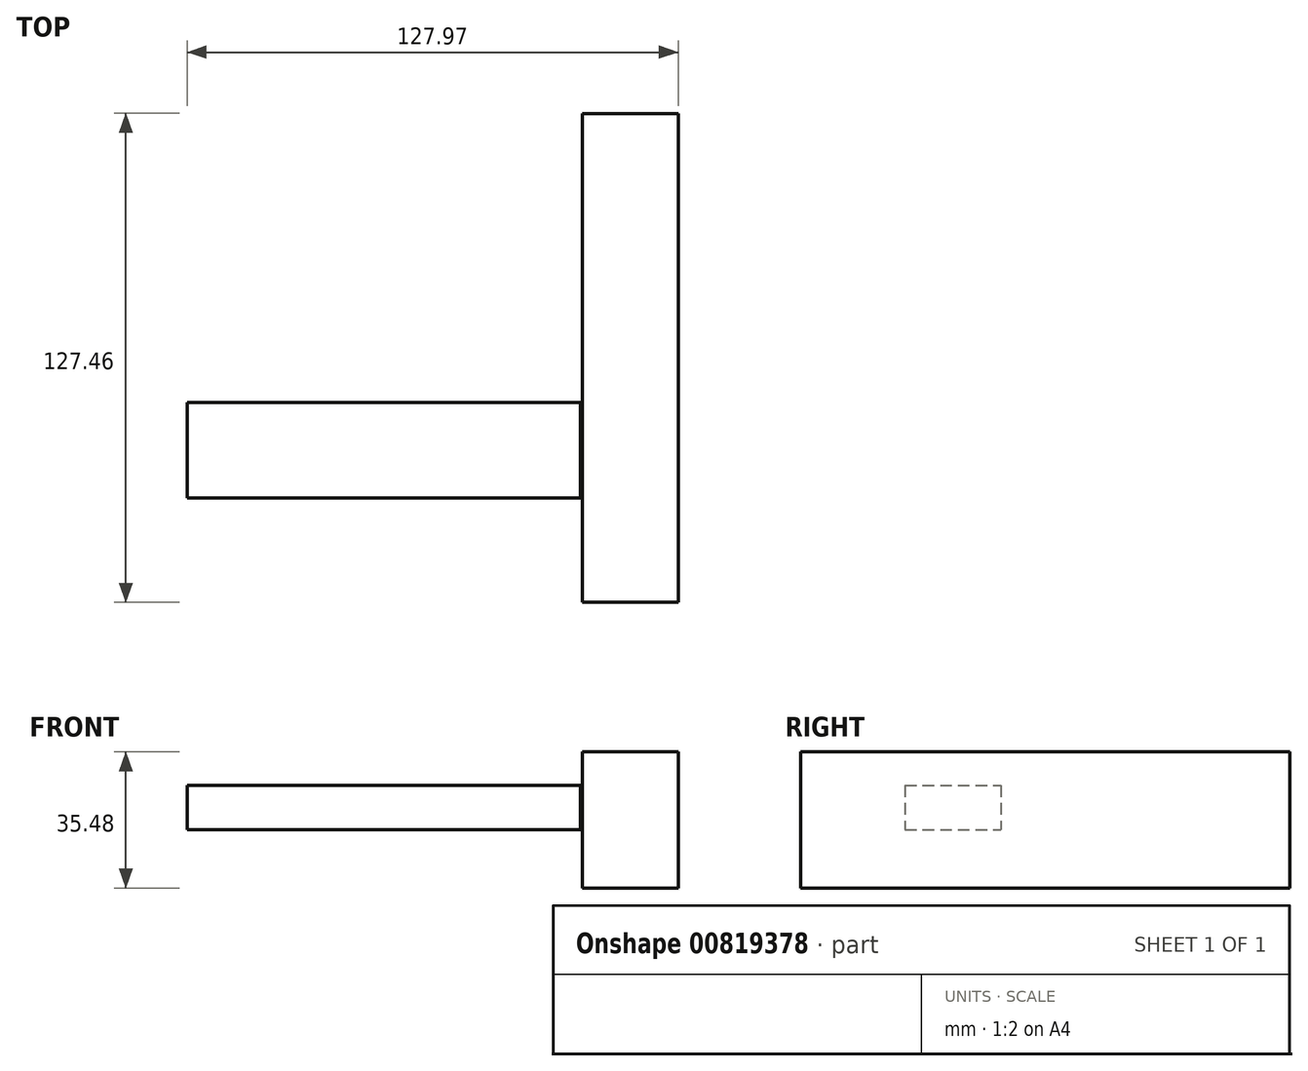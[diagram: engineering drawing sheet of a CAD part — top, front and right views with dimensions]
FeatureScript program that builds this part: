
annotation { "Feature Type Name" : "Feature", "Feature Type Description" : "" }
export const myFeature = defineFeature(function(context is Context, id is Id, definition is map)
    precondition{}
    {
        {
            var Q0;
            Q0=qCreatedBy(makeId("Right.planeOp"),FACE);
            var sketch = newSketch(context, id + "F0", { "sketchPlane" : qUnion([Q0])});
            skLineSegment(sketch, "E0.bottom", {"start": v(-52.14, 16.6) * mm, "end": v(75.32, 16.6) * mm});
            skLineSegment(sketch, "E0.top", {"start": v(-52.14, -18.9) * mm, "end": v(75.32, -18.9) * mm});
            skLineSegment(sketch, "E0.left", {"start": v(-52.14, 16.6) * mm, "end": v(-52.14, -18.9) * mm});
            skLineSegment(sketch, "E0.right", {"start": v(75.32, 16.6) * mm, "end": v(75.32, -18.9) * mm});
            skSolve(sketch);
        }
        {
            var Q0;
            Q0=makeQuery(id+"F0.imprint","IMPRINT",FACE,{"disambiguationData":[TD([[makeQuery(id+"F0.imprint","IMPRINT",EDGE,{"derivedFrom":sQuery(id+"F0.wireOp",EDGE,"E0.bottom")}),-1.0]])]});
            extrude(context, id + "F1", {"entities" : qUnion([Q0]), "endBound" : BoundingType.SYMMETRIC, "depth" : 25 * mm, "offsetDistance" : 25 * mm});
        }
        {
            var Q0;
            Q0=qCreatedBy(makeId("Front.planeOp"),FACE);
            var sketch = newSketch(context, id + "F2", { "sketchPlane" : qUnion([Q0])});
            skLineSegment(sketch, "E1.bottom", {"start": v(-13.02, 7.83) * mm, "end": v(-115.47, 7.83) * mm});
            skLineSegment(sketch, "E1.top", {"start": v(-13.02, -3.71) * mm, "end": v(-115.47, -3.71) * mm});
            skLineSegment(sketch, "E1.left", {"start": v(-13.02, 7.83) * mm, "end": v(-13.02, -3.71) * mm});
            skLineSegment(sketch, "E1.right", {"start": v(-115.47, 7.83) * mm, "end": v(-115.47, -3.71) * mm});
            skSolve(sketch);
        }
        {
            var Q0;
            Q0=makeQuery(id+"F2.imprint","IMPRINT",FACE,{"disambiguationData":[TD([[makeQuery(id+"F2.imprint","IMPRINT",EDGE,{"derivedFrom":sQuery(id+"F2.wireOp",EDGE,"E1.bottom")}),1.0]])]});
            extrude(context, id + "F3", {"entities" : qUnion([Q0]), "depth" : 25 * mm, "offsetDistance" : 25 * mm});
        }
    });
